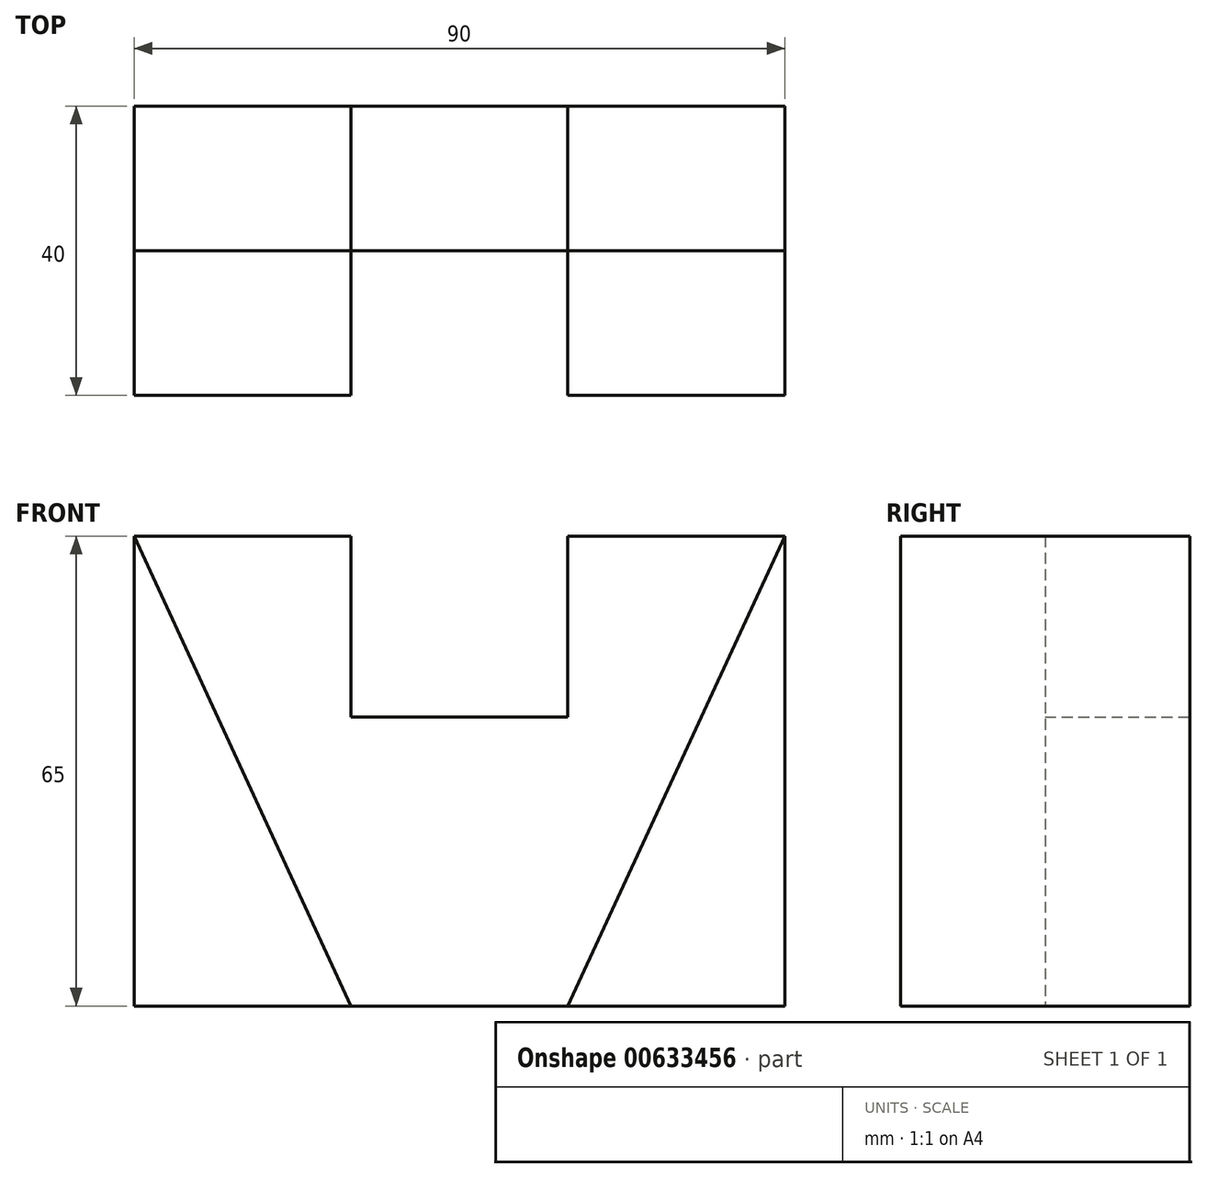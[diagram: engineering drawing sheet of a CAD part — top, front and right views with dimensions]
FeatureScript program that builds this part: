
annotation { "Feature Type Name" : "Feature", "Feature Type Description" : "" }
export const myFeature = defineFeature(function(context is Context, id is Id, definition is map)
    precondition{}
    {
        {
            var Q0;
            Q0=qCreatedBy(makeId("Front.planeOp"),FACE);
            var sketch = newSketch(context, id + "F0", { "sketchPlane" : qUnion([Q0])});
            skLineSegment(sketch, "E0.bottom", {"start": v(45, 32.5) * mm, "end": v(15, 32.5) * mm});
            skLineSegment(sketch, "E0.top", {"start": v(45, -32.5) * mm, "end": v(-45, -32.5) * mm});
            skLineSegment(sketch, "E0.left", {"start": v(45, 32.5) * mm, "end": v(45, -32.5) * mm});
            skLineSegment(sketch, "E0.right", {"start": v(-45, 32.5) * mm, "end": v(-45, -32.5) * mm});
            skPoint(sketch, "E0.middle", {"position": v(0, 0) * mm});
            skLineSegment(sketch, "E1.top", {"start": v(15, 7.5) * mm, "end": v(-15, 7.5) * mm});
            skLineSegment(sketch, "E1.left", {"start": v(15, 32.5) * mm, "end": v(15, 7.5) * mm});
            skLineSegment(sketch, "E1.right", {"start": v(-15, 32.5) * mm, "end": v(-15, 7.5) * mm});
            skPoint(sketch, "E1.middle", {"position": v(0, 20) * mm});
            skLineSegment(sketch, "E2.trimOffspring", {"start": v(-15, 32.5) * mm, "end": v(-45, 32.5) * mm});
            skSolve(sketch);
        }
        {
            var Q0;
            Q0=makeQuery(id+"F0.imprint","IMPRINT",FACE,{"disambiguationData":[TD([[makeQuery(id+"F0.imprint","IMPRINT",EDGE,{"derivedFrom":sQuery(id+"F0.wireOp",EDGE,"E0.bottom")}),1.0]])]});
            extrude(context, id + "F1", {"entities" : qUnion([Q0]), "depth" : 20 * mm, "offsetDistance" : 25 * mm});
        }
        {
            var Q0;
            Q0=makeQuery(id+"F1.opExtrude","CAP_FACE",FACE,{"disambiguationData":[OSD([sQuery(id+"F0.wireOp",EDGE,"E0.bottom"),sQuery(id+"F0.wireOp",EDGE,"E0.top"),sQuery(id+"F0.wireOp",EDGE,"E0.left"),sQuery(id+"F0.wireOp",EDGE,"E0.right"),sQuery(id+"F0.wireOp",EDGE,"E1.top"),sQuery(id+"F0.wireOp",EDGE,"E1.left"),sQuery(id+"F0.wireOp",EDGE,"E1.right"),sQuery(id+"F0.wireOp",EDGE,"E2.trimOffspring")])],"isStart":false});
            var sketch = newSketch(context, id + "F2", { "sketchPlane" : qUnion([Q0])});
            skPoint(sketch, "E3", {"position": v(-45, -32.5) * mm});
            skPoint(sketch, "E4", {"position": v(-15, -32.5) * mm});
            skPoint(sketch, "E5", {"position": v(45, -32.5) * mm});
            skPoint(sketch, "E6", {"position": v(15, -32.5) * mm});
            skLineSegment(sketch, "E7", {"start": v(-45, 32.5) * mm, "end": v(-15, -32.5) * mm});
            skLineSegment(sketch, "E8", {"start": v(45, 32.5) * mm, "end": v(15, -32.5) * mm});
            skSolve(sketch);
        }
        {
            var Q0;
            {var subQ0=sQuery(id+"F2.wireOp",EDGE,"E8");Q0=makeQuery(id+"F2.imprint","IMPRINT",FACE,{"disambiguationData":[TD([[makeQuery(id+"F2.imprint","IMPRINT",EDGE,{"derivedFrom":subQ0}),1.0]])]});}
            var Q1;
            {var subQ0=sQuery(id+"F2.wireOp",EDGE,"E7");Q1=makeQuery(id+"F2.imprint","IMPRINT",FACE,{"disambiguationData":[TD([[makeQuery(id+"F2.imprint","IMPRINT",EDGE,{"derivedFrom":subQ0}),-1.0]])]});}
            extrude(context, id + "F3", {"entities" : qUnion([Q0, Q1]), "operationType" : NewBodyOperationType.ADD, "depth" : 20 * mm, "offsetDistance" : 25 * mm});
        }
    });
